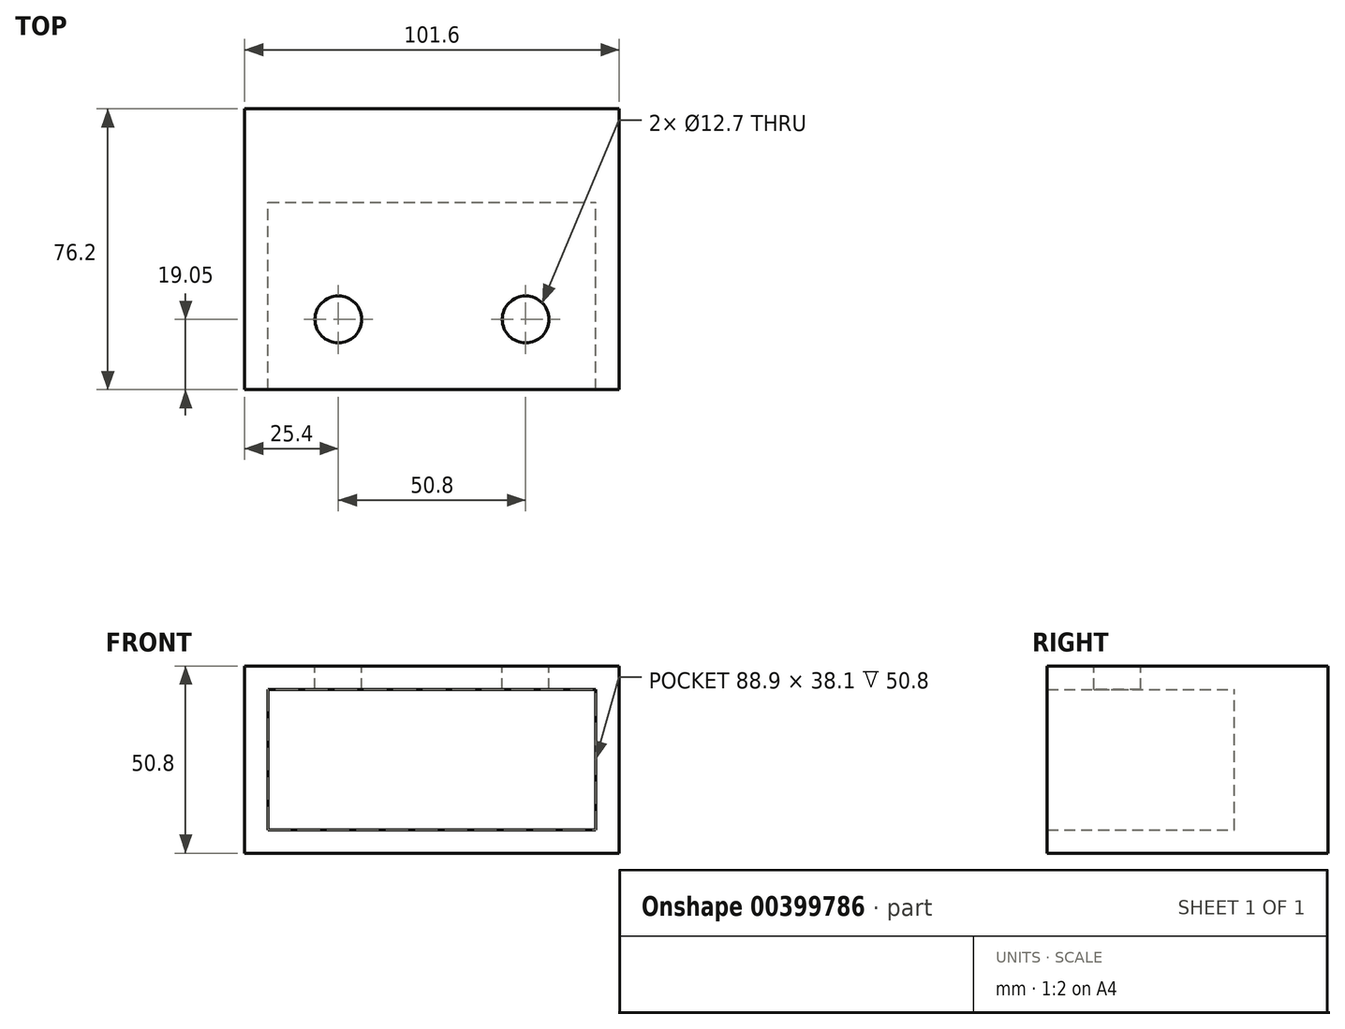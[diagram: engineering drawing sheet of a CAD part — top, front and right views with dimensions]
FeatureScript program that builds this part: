
annotation { "Feature Type Name" : "Feature", "Feature Type Description" : "" }
export const myFeature = defineFeature(function(context is Context, id is Id, definition is map)
    precondition{}
    {
        {
            var Q0;
            Q0=qCreatedBy(makeId("Front.planeOp"),FACE);
            var sketch = newSketch(context, id + "F0", { "sketchPlane" : qUnion([Q0])});
            skLineSegment(sketch, "E0.bottom", {"start": v(0, 0) * mm, "end": v(101.6, 0) * mm});
            skLineSegment(sketch, "E0.top", {"start": v(0, 50.8) * mm, "end": v(101.6, 50.8) * mm});
            skLineSegment(sketch, "E0.left", {"start": v(0, 0) * mm, "end": v(0, 50.8) * mm});
            skLineSegment(sketch, "E0.right", {"start": v(101.6, 0) * mm, "end": v(101.6, 50.8) * mm});
            skLineSegment(sketch, "E1.0", {"start": v(6.35, 44.45) * mm, "end": v(95.25, 44.45) * mm});
            skLineSegment(sketch, "E1.1", {"start": v(6.35, 6.35) * mm, "end": v(6.35, 44.45) * mm});
            skLineSegment(sketch, "E1.2", {"start": v(6.35, 6.35) * mm, "end": v(95.25, 6.35) * mm});
            skLineSegment(sketch, "E1.3", {"start": v(95.25, 6.35) * mm, "end": v(95.25, 44.45) * mm});
            skSolve(sketch);
        }
        {
            var Q0;
            Q0 = qSketchRegion(id + "F0", true);
            extrude(context, id + "F1", {"entities" : qUnion([Q0]), "depth" : 76.2 * mm});
        }
        {
            var Q0;
            Q0=qCreatedBy(makeId("Front.planeOp"),FACE);
            var sketch = newSketch(context, id + "F2", { "sketchPlane" : qUnion([Q0])});
            skLineSegment(sketch, "E2.bottom", {"start": v(6.35, 6.35) * mm, "end": v(95.25, 6.35) * mm});
            skLineSegment(sketch, "E2.top", {"start": v(6.35, 44.45) * mm, "end": v(95.25, 44.45) * mm});
            skLineSegment(sketch, "E2.left", {"start": v(6.35, 6.35) * mm, "end": v(6.35, 44.45) * mm});
            skLineSegment(sketch, "E2.right", {"start": v(95.25, 6.35) * mm, "end": v(95.25, 44.45) * mm});
            skSolve(sketch);
        }
        {
            var Q0;
            Q0 = qSketchRegion(id + "F2", true);
            extrude(context, id + "F3", {"entities" : qUnion([Q0]), "operationType" : NewBodyOperationType.ADD, "depth" : 25.4 * mm});
        }
        {
            var Q0;
            Q0=makeQuery(id+"F1.opExtrude","SWEPT_FACE",FACE,{"disambiguationData":[OSD([sQuery(id+"F0.wireOp",EDGE,"E0.top")])]});
            var sketch = newSketch(context, id + "F4", { "sketchPlane" : qUnion([Q0])});
            skCircle(sketch, "E3", {"center": v(25.4, -57.15) * mm, "radius": 6.35 * mm});
            skCircle(sketch, "E4", {"center": v(76.2, -57.15) * mm, "radius": 6.35 * mm});
            skSolve(sketch);
        }
        {
            var Q0;
            Q0 = qSketchRegion(id + "F4", true);
            extrude(context, id + "F5", {"entities" : qUnion([Q0]), "operationType" : NewBodyOperationType.REMOVE, "oppositeDirection" : true, "depth" : 25.4 * mm});
        }
    });
